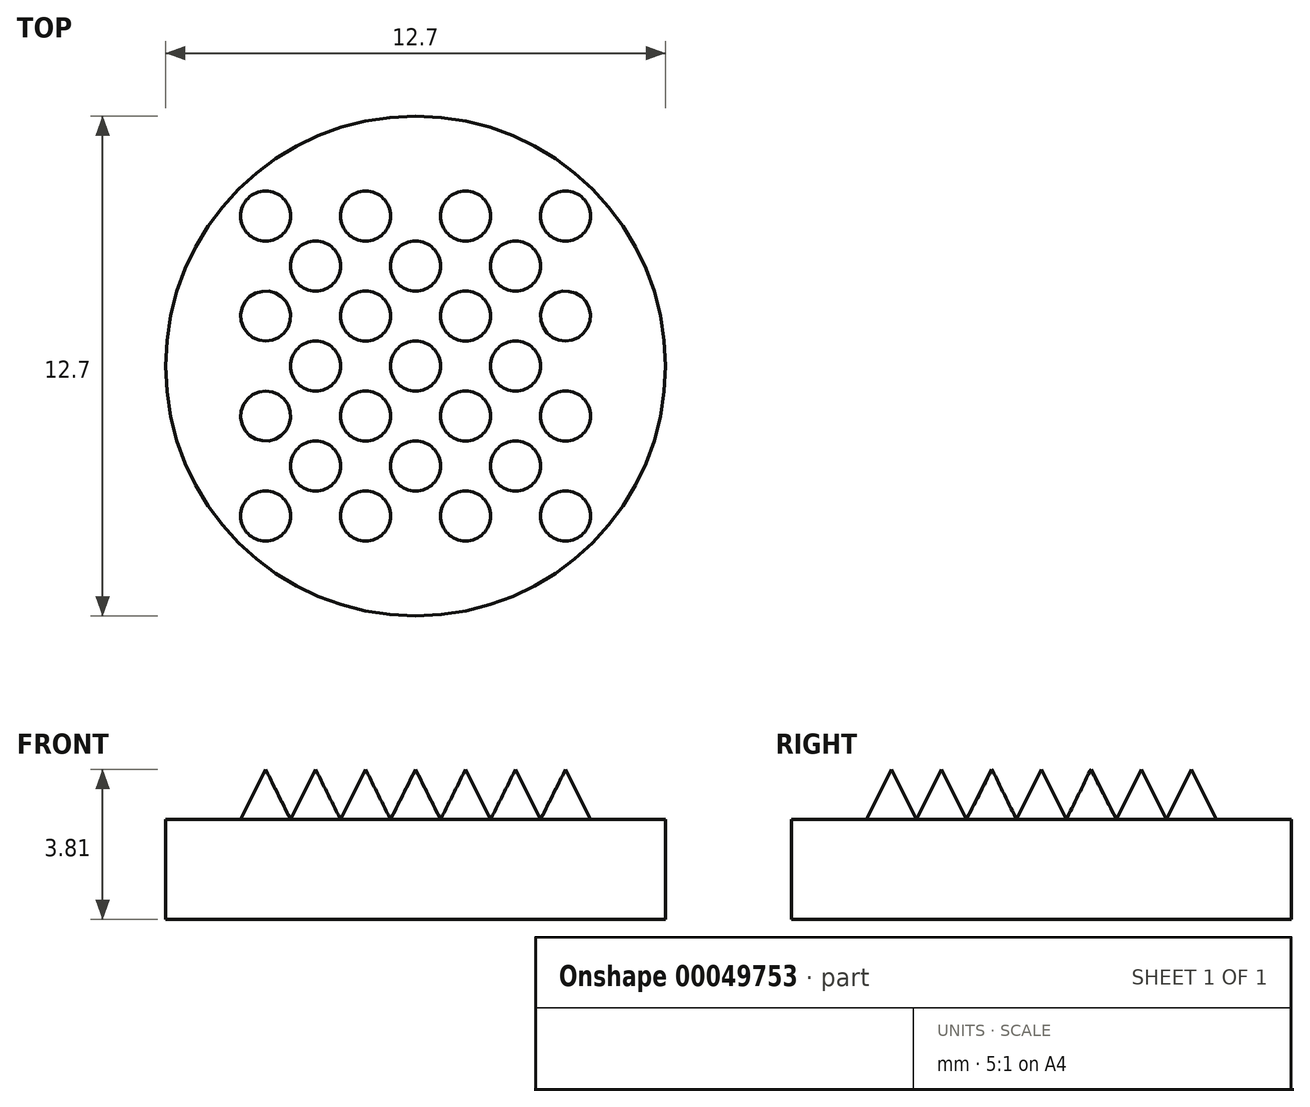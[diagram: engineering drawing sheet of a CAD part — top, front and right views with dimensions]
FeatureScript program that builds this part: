
annotation { "Feature Type Name" : "Feature", "Feature Type Description" : "" }
export const myFeature = defineFeature(function(context is Context, id is Id, definition is map)
    precondition{}
    {
        {
            var Q0;
            Q0=qCreatedBy(makeId("Top.planeOp"),FACE);
            var sketch = newSketch(context, id + "F0", { "sketchPlane" : qUnion([Q0])});
            skCircle(sketch, "E0", {"center": v(0, 0) * mm, "radius": 6.35 * mm});
            skSolve(sketch);
        }
        {
            var Q0;
            Q0=qCreatedBy(makeId("Top.planeOp"),FACE);
            var sketch = newSketch(context, id + "F1", { "sketchPlane" : qUnion([Q0])});
            skCircle(sketch, "E1", {"center": v(0, 0) * mm, "radius": 0.64 * mm});
            skCircle(sketch, "E2", {"center": v(1.27, 0) * mm, "radius": 0.64 * mm});
            skCircle(sketch, "E3", {"center": v(2.54, 0) * mm, "radius": 0.64 * mm});
            skCircle(sketch, "E4", {"center": v(1.27, -1.27) * mm, "radius": 0.64 * mm});
            skCircle(sketch, "E5", {"center": v(2.54, -1.27) * mm, "radius": 0.64 * mm});
            skCircle(sketch, "E6", {"center": v(1.27, -2.54) * mm, "radius": 0.64 * mm});
            skCircle(sketch, "E7", {"center": v(1.27, -3.81) * mm, "radius": 0.64 * mm});
            skCircle(sketch, "E8", {"center": v(2.54, -2.54) * mm, "radius": 0.64 * mm});
            skCircle(sketch, "E9", {"center": v(2.54, -3.81) * mm, "radius": 0.64 * mm});
            skCircle(sketch, "E10", {"center": v(0, -1.27) * mm, "radius": 0.64 * mm});
            skCircle(sketch, "E11", {"center": v(0, -2.54) * mm, "radius": 0.64 * mm});
            skCircle(sketch, "E12", {"center": v(0, -3.81) * mm, "radius": 0.64 * mm});
            skCircle(sketch, "E13", {"center": v(3.81, 0) * mm, "radius": 0.64 * mm});
            skCircle(sketch, "E14", {"center": v(3.81, -1.27) * mm, "radius": 0.64 * mm});
            skCircle(sketch, "E15", {"center": v(3.81, -2.54) * mm, "radius": 0.64 * mm});
            skCircle(sketch, "E16", {"center": v(3.81, -3.81) * mm, "radius": 0.64 * mm});
            skSolve(sketch);
        }
        {
            var Q0;
            Q0=makeQuery(id+"F1.imprint","IMPRINT",FACE,{"disambiguationData":[TD([[makeQuery(id+"F1.imprint","IMPRINT",EDGE,{"derivedFrom":sQuery(id+"F1.wireOp",EDGE,"E1")}),1.0]])]});
            cPlane(context, id + "F2", {"entities" : qUnion([Q0]), "cplaneType" : CPlaneType.OFFSET, "offset" : 1.27 * mm, "width" : 152.4 * mm, "height" : 152.4 * mm});
        }
        {
            var Q0;
            Q0=qCreatedBy(id+"F2.planeOp",FACE);
            var sketch = newSketch(context, id + "F3", { "sketchPlane" : qUnion([Q0])});
            skPoint(sketch, "E17", {"position": v(0, 0) * mm});
            skPoint(sketch, "E18", {"position": v(0, -1.27) * mm});
            skPoint(sketch, "E19", {"position": v(0, -2.54) * mm});
            skPoint(sketch, "E20", {"position": v(1.27, 0) * mm});
            skPoint(sketch, "E21", {"position": v(1.27, -1.27) * mm});
            skPoint(sketch, "E22", {"position": v(1.27, -2.54) * mm});
            skPoint(sketch, "E23", {"position": v(1.27, -3.81) * mm});
            skPoint(sketch, "E24", {"position": v(2.54, 0) * mm});
            skPoint(sketch, "E25", {"position": v(2.54, -1.27) * mm});
            skPoint(sketch, "E26", {"position": v(2.54, -2.54) * mm});
            skPoint(sketch, "E27", {"position": v(2.54, -3.81) * mm});
            skPoint(sketch, "E28", {"position": v(0, -3.81) * mm});
            skPoint(sketch, "E29", {"position": v(3.81, 0) * mm});
            skPoint(sketch, "E30", {"position": v(3.8, -1.25) * mm});
            skPoint(sketch, "E31", {"position": v(3.81, -2.51) * mm});
            skPoint(sketch, "E32", {"position": v(3.81, -3.81) * mm});
            skSolve(sketch);
        }
        {
            var Q0;
            {var subQ0=sQuery(id+"F1.wireOp",EDGE,"E1");var subQ1=makeQuery(id+"F1.imprint","INTERSECT",VERTEX,{"derivedFrom":[subQ0,sQuery(id+"F1.wireOp",EDGE,"E2")]});Q0=makeQuery(id+"F1.imprint","IMPRINT",FACE,{"disambiguationData":[TD([[makeQuery(id+"F1.imprint","IMPRINT",EDGE,{"disambiguationData":[TD([[subQ1,-1.0]])],"derivedFrom":subQ0}),1.0]])]});}
            var Q1;
            Q1=sQuery(id+"F3.wireOp",VERTEX,"E17");
            loft(context, id + "F4", {"sheetProfilesArray" : [{ "sheetProfileEntities" : qUnion([Q0]) }, { "sheetProfileEntities" : qUnion([Q1]) }]});
        }
        {
            var Q0;
            Q0=makeQuery(id+"F0.imprint","IMPRINT",FACE,{"disambiguationData":[TD([[makeQuery(id+"F0.imprint","IMPRINT",EDGE,{"derivedFrom":sQuery(id+"F0.wireOp",EDGE,"E0")}),1.0]])]});
            extrude(context, id + "F5", {"entities" : qUnion([Q0]), "oppositeDirection" : true, "depth" : 2.54 * mm});
        }
        {
            var Q1;
            {var subQ0=sQuery(id+"F1.wireOp",EDGE,"E11");var subQ1=makeQuery(id+"F1.imprint","INTERSECT",VERTEX,{"derivedFrom":[sQuery(id+"F1.wireOp",EDGE,"E10"),subQ0]});Q1=makeQuery(id+"F1.imprint","IMPRINT",FACE,{"disambiguationData":[TD([[makeQuery(id+"F1.imprint","IMPRINT",EDGE,{"disambiguationData":[TD([[subQ1,1.0]])],"derivedFrom":subQ0}),1.0]])]});}
            var Q2;
            Q2=sQuery(id+"F3.wireOp",VERTEX,"E19");
            loft(context, id + "F6", {"sheetProfilesArray" : [{ "sheetProfileEntities" : qUnion([Q1]) }, { "sheetProfileEntities" : qUnion([Q2]) }]});
        }
        {
            var Q1;
            {var subQ0=sQuery(id+"F1.wireOp",EDGE,"E4");var subQ1=makeQuery(id+"F1.imprint","INTERSECT",VERTEX,{"derivedFrom":[sQuery(id+"F1.wireOp",EDGE,"E2"),subQ0]});Q1=makeQuery(id+"F1.imprint","IMPRINT",FACE,{"disambiguationData":[TD([[makeQuery(id+"F1.imprint","IMPRINT",EDGE,{"disambiguationData":[TD([[subQ1,1.0]])],"derivedFrom":subQ0}),1.0]])]});}
            var Q2;
            Q2=sQuery(id+"F3.wireOp",VERTEX,"E21");
            loft(context, id + "F7", {"sheetProfilesArray" : [{ "sheetProfileEntities" : qUnion([Q1]) }, { "sheetProfileEntities" : qUnion([Q2]) }]});
        }
        {
            var Q1;
            {var subQ0=sQuery(id+"F1.wireOp",EDGE,"E7");var subQ1=makeQuery(id+"F1.imprint","INTERSECT",VERTEX,{"derivedFrom":[subQ0,sQuery(id+"F1.wireOp",EDGE,"E9")]});Q1=makeQuery(id+"F1.imprint","IMPRINT",FACE,{"disambiguationData":[TD([[makeQuery(id+"F1.imprint","IMPRINT",EDGE,{"disambiguationData":[TD([[subQ1,-1.0]])],"derivedFrom":subQ0}),1.0]])]});}
            var Q2;
            Q2=sQuery(id+"F3.wireOp",VERTEX,"E23");
            loft(context, id + "F8", {"sheetProfilesArray" : [{ "sheetProfileEntities" : qUnion([Q1]) }, { "sheetProfileEntities" : qUnion([Q2]) }]});
        }
        {
            var Q1;
            {var subQ0=sQuery(id+"F1.wireOp",EDGE,"E3");var subQ1=makeQuery(id+"F1.imprint","INTERSECT",VERTEX,{"derivedFrom":[sQuery(id+"F1.wireOp",EDGE,"E2"),subQ0]});Q1=makeQuery(id+"F1.imprint","IMPRINT",FACE,{"disambiguationData":[TD([[makeQuery(id+"F1.imprint","IMPRINT",EDGE,{"disambiguationData":[TD([[subQ1,-1.0]])],"derivedFrom":subQ0}),1.0]])]});}
            var Q2;
            Q2=sQuery(id+"F3.wireOp",VERTEX,"E24");
            loft(context, id + "F9", {"sheetProfilesArray" : [{ "sheetProfileEntities" : qUnion([Q1]) }, { "sheetProfileEntities" : qUnion([Q2]) }]});
        }
        {
            var Q1;
            {var subQ0=sQuery(id+"F1.wireOp",EDGE,"E8");var subQ1=makeQuery(id+"F1.imprint","INTERSECT",VERTEX,{"derivedFrom":[sQuery(id+"F1.wireOp",EDGE,"E5"),subQ0]});Q1=makeQuery(id+"F1.imprint","IMPRINT",FACE,{"disambiguationData":[TD([[makeQuery(id+"F1.imprint","IMPRINT",EDGE,{"disambiguationData":[TD([[subQ1,-1.0]])],"derivedFrom":subQ0}),1.0]])]});}
            var Q2;
            Q2=sQuery(id+"F3.wireOp",VERTEX,"E26");
            loft(context, id + "F10", {"sheetProfilesArray" : [{ "sheetProfileEntities" : qUnion([Q1]) }, { "sheetProfileEntities" : qUnion([Q2]) }]});
        }
        {
            var Q1;
            {var subQ0=sQuery(id+"F1.wireOp",EDGE,"E14");var subQ1=makeQuery(id+"F1.imprint","INTERSECT",VERTEX,{"derivedFrom":[sQuery(id+"F1.wireOp",EDGE,"E13"),subQ0]});Q1=makeQuery(id+"F1.imprint","IMPRINT",FACE,{"disambiguationData":[TD([[makeQuery(id+"F1.imprint","IMPRINT",EDGE,{"disambiguationData":[TD([[subQ1,-1.0]])],"derivedFrom":subQ0}),1.0]])]});}
            var Q2;
            Q2=sQuery(id+"F3.wireOp",VERTEX,"E30");
            loft(context, id + "F11", {"sheetProfilesArray" : [{ "sheetProfileEntities" : qUnion([Q1]) }, { "sheetProfileEntities" : qUnion([Q2]) }]});
        }
        {
            var Q1;
            {var subQ0=sQuery(id+"F1.wireOp",EDGE,"E16");var subQ1=makeQuery(id+"F1.imprint","INTERSECT",VERTEX,{"derivedFrom":[sQuery(id+"F1.wireOp",EDGE,"E9"),subQ0]});Q1=makeQuery(id+"F1.imprint","IMPRINT",FACE,{"disambiguationData":[TD([[makeQuery(id+"F1.imprint","IMPRINT",EDGE,{"disambiguationData":[TD([[subQ1,1.0]])],"derivedFrom":subQ0}),1.0]])]});}
            var Q2;
            Q2=sQuery(id+"F3.wireOp",VERTEX,"E32");
            loft(context, id + "F12", {"sheetProfilesArray" : [{ "sheetProfileEntities" : qUnion([Q1]) }, { "sheetProfileEntities" : qUnion([Q2]) }]});
        }
        {
            var Q0;
            {var subQ0=sQuery(id+"F1.wireOp",EDGE,"E1");var subQ1=makeQuery(id+"F1.imprint","INTERSECT",VERTEX,{"derivedFrom":[subQ0,sQuery(id+"F1.wireOp",EDGE,"E2")]});Q0=makeQuery(id+"F4.opLoft","SWEPT_BODY",BODY,{"disambiguationData":[OSD([makeQuery(id+"F1.imprint","IMPRINT",FACE,{"disambiguationData":[TD([[makeQuery(id+"F1.imprint","IMPRINT",EDGE,{"disambiguationData":[TD([[subQ1,-1.0]])],"derivedFrom":subQ0}),1.0]])]}),sQuery(id+"F3.wireOp",VERTEX,"E17")])]});}
            var Q1;
            {var subQ0=sQuery(id+"F1.wireOp",EDGE,"E10");var subQ1=makeQuery(id+"F1.imprint","INTERSECT",VERTEX,{"derivedFrom":[sQuery(id+"F1.wireOp",EDGE,"E1"),subQ0]});Q1=makeQuery(id+"F5vqhCHL6ANKIna_3.opLoft","SWEPT_BODY",BODY,{"disambiguationData":[OSD([makeQuery(id+"F1.imprint","IMPRINT",FACE,{"disambiguationData":[TD([[makeQuery(id+"F1.imprint","IMPRINT",EDGE,{"disambiguationData":[TD([[subQ1,1.0]])],"derivedFrom":subQ0}),1.0]])]}),sQuery(id+"F3.wireOp",VERTEX,"E18")])]});}
            var Q2;
            {var subQ0=sQuery(id+"F1.wireOp",EDGE,"E11");var subQ1=makeQuery(id+"F1.imprint","INTERSECT",VERTEX,{"derivedFrom":[sQuery(id+"F1.wireOp",EDGE,"E10"),subQ0]});Q2=makeQuery(id+"F6.opLoft","SWEPT_BODY",BODY,{"disambiguationData":[OSD([makeQuery(id+"F1.imprint","IMPRINT",FACE,{"disambiguationData":[TD([[makeQuery(id+"F1.imprint","IMPRINT",EDGE,{"disambiguationData":[TD([[subQ1,1.0]])],"derivedFrom":subQ0}),1.0]])]}),sQuery(id+"F3.wireOp",VERTEX,"E19")])]});}
            var Q3;
            {var subQ0=sQuery(id+"F1.wireOp",EDGE,"E12");var subQ1=makeQuery(id+"F1.imprint","INTERSECT",VERTEX,{"derivedFrom":[sQuery(id+"F1.wireOp",EDGE,"E7"),subQ0]});Q3=makeQuery(id+"FCgEybhU7v2E6e9_3.opLoft","SWEPT_BODY",BODY,{"disambiguationData":[OSD([makeQuery(id+"F1.imprint","IMPRINT",FACE,{"disambiguationData":[TD([[makeQuery(id+"F1.imprint","IMPRINT",EDGE,{"disambiguationData":[TD([[subQ1,-1.0]])],"derivedFrom":subQ0}),1.0]])]}),sQuery(id+"F3.wireOp",VERTEX,"E28")])]});}
            var Q4;
            {var subQ0=sQuery(id+"F1.wireOp",EDGE,"E7");var subQ1=makeQuery(id+"F1.imprint","INTERSECT",VERTEX,{"derivedFrom":[subQ0,sQuery(id+"F1.wireOp",EDGE,"E9")]});Q4=makeQuery(id+"F8.opLoft","SWEPT_BODY",BODY,{"disambiguationData":[OSD([makeQuery(id+"F1.imprint","IMPRINT",FACE,{"disambiguationData":[TD([[makeQuery(id+"F1.imprint","IMPRINT",EDGE,{"disambiguationData":[TD([[subQ1,-1.0]])],"derivedFrom":subQ0}),1.0]])]}),sQuery(id+"F3.wireOp",VERTEX,"E23")])]});}
            var Q5;
            {var subQ0=sQuery(id+"F1.wireOp",EDGE,"E6");var subQ1=makeQuery(id+"F1.imprint","INTERSECT",VERTEX,{"derivedFrom":[sQuery(id+"F1.wireOp",EDGE,"E4"),subQ0]});Q5=makeQuery(id+"FVhk51bG2k9nDs2_3.opLoft","SWEPT_BODY",BODY,{"disambiguationData":[OSD([makeQuery(id+"F1.imprint","IMPRINT",FACE,{"disambiguationData":[TD([[makeQuery(id+"F1.imprint","IMPRINT",EDGE,{"disambiguationData":[TD([[subQ1,1.0]])],"derivedFrom":subQ0}),1.0]])]}),sQuery(id+"F3.wireOp",VERTEX,"E22")])]});}
            var Q6;
            {var subQ0=sQuery(id+"F1.wireOp",EDGE,"E4");var subQ1=makeQuery(id+"F1.imprint","INTERSECT",VERTEX,{"derivedFrom":[sQuery(id+"F1.wireOp",EDGE,"E2"),subQ0]});Q6=makeQuery(id+"F7.opLoft","SWEPT_BODY",BODY,{"disambiguationData":[OSD([makeQuery(id+"F1.imprint","IMPRINT",FACE,{"disambiguationData":[TD([[makeQuery(id+"F1.imprint","IMPRINT",EDGE,{"disambiguationData":[TD([[subQ1,1.0]])],"derivedFrom":subQ0}),1.0]])]}),sQuery(id+"F3.wireOp",VERTEX,"E21")])]});}
            var Q7;
            {var subQ0=sQuery(id+"F1.wireOp",EDGE,"E2");var subQ1=makeQuery(id+"F1.imprint","INTERSECT",VERTEX,{"derivedFrom":[sQuery(id+"F1.wireOp",EDGE,"E1"),subQ0]});Q7=makeQuery(id+"F8jPV2Md5eXivMf_3.opLoft","SWEPT_BODY",BODY,{"disambiguationData":[OSD([makeQuery(id+"F1.imprint","IMPRINT",FACE,{"disambiguationData":[TD([[makeQuery(id+"F1.imprint","IMPRINT",EDGE,{"disambiguationData":[TD([[subQ1,1.0]])],"derivedFrom":subQ0}),1.0]])]}),sQuery(id+"F3.wireOp",VERTEX,"E20")])]});}
            var Q8;
            {var subQ0=sQuery(id+"F1.wireOp",EDGE,"E13");var subQ1=makeQuery(id+"F1.imprint","INTERSECT",VERTEX,{"derivedFrom":[sQuery(id+"F1.wireOp",EDGE,"E3"),subQ0]});Q8=makeQuery(id+"FrQLQlC9Cd4ulGg_3.opLoft","SWEPT_BODY",BODY,{"disambiguationData":[OSD([makeQuery(id+"F1.imprint","IMPRINT",FACE,{"disambiguationData":[TD([[makeQuery(id+"F1.imprint","IMPRINT",EDGE,{"disambiguationData":[TD([[subQ1,-1.0]])],"derivedFrom":subQ0}),1.0]])]}),sQuery(id+"F3.wireOp",VERTEX,"E29")])]});}
            var Q9;
            {var subQ0=sQuery(id+"F1.wireOp",EDGE,"E3");var subQ1=makeQuery(id+"F1.imprint","INTERSECT",VERTEX,{"derivedFrom":[sQuery(id+"F1.wireOp",EDGE,"E2"),subQ0]});Q9=makeQuery(id+"F9.opLoft","SWEPT_BODY",BODY,{"disambiguationData":[OSD([makeQuery(id+"F1.imprint","IMPRINT",FACE,{"disambiguationData":[TD([[makeQuery(id+"F1.imprint","IMPRINT",EDGE,{"disambiguationData":[TD([[subQ1,1.0]])],"derivedFrom":subQ0}),1.0]])]}),sQuery(id+"F3.wireOp",VERTEX,"E24")])]});}
            var Q10;
            {var subQ0=sQuery(id+"F1.wireOp",EDGE,"E5");var subQ1=makeQuery(id+"F1.imprint","INTERSECT",VERTEX,{"derivedFrom":[sQuery(id+"F1.wireOp",EDGE,"E3"),subQ0]});Q10=makeQuery(id+"FChkki0fDYVnrYv_3.opLoft","SWEPT_BODY",BODY,{"disambiguationData":[OSD([makeQuery(id+"F1.imprint","IMPRINT",FACE,{"disambiguationData":[TD([[makeQuery(id+"F1.imprint","IMPRINT",EDGE,{"disambiguationData":[TD([[subQ1,1.0]])],"derivedFrom":subQ0}),1.0]])]}),sQuery(id+"F3.wireOp",VERTEX,"E25")])]});}
            var Q11;
            {var subQ0=sQuery(id+"F1.wireOp",EDGE,"E14");var subQ1=makeQuery(id+"F1.imprint","INTERSECT",VERTEX,{"derivedFrom":[sQuery(id+"F1.wireOp",EDGE,"E13"),subQ0]});Q11=makeQuery(id+"F11.opLoft","SWEPT_BODY",BODY,{"disambiguationData":[OSD([makeQuery(id+"F1.imprint","IMPRINT",FACE,{"disambiguationData":[TD([[makeQuery(id+"F1.imprint","IMPRINT",EDGE,{"disambiguationData":[TD([[subQ1,-1.0]])],"derivedFrom":subQ0}),1.0]])]}),sQuery(id+"F3.wireOp",VERTEX,"E30")])]});}
            var Q12;
            {var subQ0=sQuery(id+"F1.wireOp",EDGE,"E15");var subQ1=makeQuery(id+"F1.imprint","INTERSECT",VERTEX,{"derivedFrom":[sQuery(id+"F1.wireOp",EDGE,"E14"),subQ0]});Q12=makeQuery(id+"Fu73TNwijkVTWP9_3.opLoft","SWEPT_BODY",BODY,{"disambiguationData":[OSD([makeQuery(id+"F1.imprint","IMPRINT",FACE,{"disambiguationData":[TD([[makeQuery(id+"F1.imprint","IMPRINT",EDGE,{"disambiguationData":[TD([[subQ1,-1.0]])],"derivedFrom":subQ0}),1.0]])]}),sQuery(id+"F3.wireOp",VERTEX,"E31")])]});}
            var Q13;
            {var subQ0=sQuery(id+"F1.wireOp",EDGE,"E8");var subQ1=makeQuery(id+"F1.imprint","INTERSECT",VERTEX,{"derivedFrom":[sQuery(id+"F1.wireOp",EDGE,"E5"),subQ0]});Q13=makeQuery(id+"F10.opLoft","SWEPT_BODY",BODY,{"disambiguationData":[OSD([makeQuery(id+"F1.imprint","IMPRINT",FACE,{"disambiguationData":[TD([[makeQuery(id+"F1.imprint","IMPRINT",EDGE,{"disambiguationData":[TD([[subQ1,1.0]])],"derivedFrom":subQ0}),1.0]])]}),sQuery(id+"F3.wireOp",VERTEX,"E26")])]});}
            var Q14;
            {var subQ0=sQuery(id+"F1.wireOp",EDGE,"E9");var subQ1=makeQuery(id+"F1.imprint","INTERSECT",VERTEX,{"derivedFrom":[subQ0,sQuery(id+"F1.wireOp",EDGE,"E16")]});Q14=makeQuery(id+"FI5Cp5ij7l5rHYo_3.opLoft","SWEPT_BODY",BODY,{"disambiguationData":[OSD([makeQuery(id+"F1.imprint","IMPRINT",FACE,{"disambiguationData":[TD([[makeQuery(id+"F1.imprint","IMPRINT",EDGE,{"disambiguationData":[TD([[subQ1,-1.0]])],"derivedFrom":subQ0}),1.0]])]}),sQuery(id+"F3.wireOp",VERTEX,"E27")])]});}
            var Q15;
            {var subQ0=sQuery(id+"F1.wireOp",EDGE,"E16");var subQ1=makeQuery(id+"F1.imprint","INTERSECT",VERTEX,{"derivedFrom":[sQuery(id+"F1.wireOp",EDGE,"E9"),subQ0]});Q15=makeQuery(id+"F12.opLoft","SWEPT_BODY",BODY,{"disambiguationData":[OSD([makeQuery(id+"F1.imprint","IMPRINT",FACE,{"disambiguationData":[TD([[makeQuery(id+"F1.imprint","IMPRINT",EDGE,{"disambiguationData":[TD([[subQ1,1.0]])],"derivedFrom":subQ0}),1.0]])]}),sQuery(id+"F3.wireOp",VERTEX,"E32")])]});}
            var Q16;
            Q16=qCreatedBy(makeId("Right.planeOp"),FACE);
            mirror(context, id + "F13", {"entities" : qUnion([Q0, Q1, Q2, Q3, Q4, Q5, Q6, Q7, Q8, Q9, Q10, Q11, Q12, Q13, Q14, Q15]), "mirrorPlane" : qUnion([Q16])});
        }
        {
            var Q0;
            {var subQ0=sQuery(id+"F1.wireOp",EDGE,"E13");var subQ1=makeQuery(id+"F1.imprint","INTERSECT",VERTEX,{"derivedFrom":[sQuery(id+"F1.wireOp",EDGE,"E3"),subQ0]});Q0=makeQuery(id+"F13.opPattern","COPY",BODY,{"derivedFrom":makeQuery(id+"FrQLQlC9Cd4ulGg_3.opLoft","SWEPT_BODY",BODY,{"disambiguationData":[OSD([makeQuery(id+"F1.imprint","IMPRINT",FACE,{"disambiguationData":[TD([[makeQuery(id+"F1.imprint","IMPRINT",EDGE,{"disambiguationData":[TD([[subQ1,-1.0]])],"derivedFrom":subQ0}),1.0]])]}),sQuery(id+"F3.wireOp",VERTEX,"E29")])]}),"instanceName":"1"});}
            var Q1;
            {var subQ0=sQuery(id+"F1.wireOp",EDGE,"E14");var subQ1=makeQuery(id+"F1.imprint","INTERSECT",VERTEX,{"derivedFrom":[sQuery(id+"F1.wireOp",EDGE,"E13"),subQ0]});Q1=makeQuery(id+"F13.opPattern","COPY",BODY,{"derivedFrom":makeQuery(id+"F11.opLoft","SWEPT_BODY",BODY,{"disambiguationData":[OSD([makeQuery(id+"F1.imprint","IMPRINT",FACE,{"disambiguationData":[TD([[makeQuery(id+"F1.imprint","IMPRINT",EDGE,{"disambiguationData":[TD([[subQ1,-1.0]])],"derivedFrom":subQ0}),1.0]])]}),sQuery(id+"F3.wireOp",VERTEX,"E30")])]}),"instanceName":"1"});}
            var Q2;
            {var subQ0=sQuery(id+"F1.wireOp",EDGE,"E15");var subQ1=makeQuery(id+"F1.imprint","INTERSECT",VERTEX,{"derivedFrom":[sQuery(id+"F1.wireOp",EDGE,"E14"),subQ0]});Q2=makeQuery(id+"F13.opPattern","COPY",BODY,{"derivedFrom":makeQuery(id+"Fu73TNwijkVTWP9_3.opLoft","SWEPT_BODY",BODY,{"disambiguationData":[OSD([makeQuery(id+"F1.imprint","IMPRINT",FACE,{"disambiguationData":[TD([[makeQuery(id+"F1.imprint","IMPRINT",EDGE,{"disambiguationData":[TD([[subQ1,-1.0]])],"derivedFrom":subQ0}),1.0]])]}),sQuery(id+"F3.wireOp",VERTEX,"E31")])]}),"instanceName":"1"});}
            var Q3;
            {var subQ0=sQuery(id+"F1.wireOp",EDGE,"E16");var subQ1=makeQuery(id+"F1.imprint","INTERSECT",VERTEX,{"derivedFrom":[sQuery(id+"F1.wireOp",EDGE,"E9"),subQ0]});Q3=makeQuery(id+"F13.opPattern","COPY",BODY,{"derivedFrom":makeQuery(id+"F12.opLoft","SWEPT_BODY",BODY,{"disambiguationData":[OSD([makeQuery(id+"F1.imprint","IMPRINT",FACE,{"disambiguationData":[TD([[makeQuery(id+"F1.imprint","IMPRINT",EDGE,{"disambiguationData":[TD([[subQ1,1.0]])],"derivedFrom":subQ0}),1.0]])]}),sQuery(id+"F3.wireOp",VERTEX,"E32")])]}),"instanceName":"1"});}
            var Q4;
            {var subQ0=sQuery(id+"F1.wireOp",EDGE,"E9");var subQ1=makeQuery(id+"F1.imprint","INTERSECT",VERTEX,{"derivedFrom":[subQ0,sQuery(id+"F1.wireOp",EDGE,"E16")]});Q4=makeQuery(id+"F13.opPattern","COPY",BODY,{"derivedFrom":makeQuery(id+"FI5Cp5ij7l5rHYo_3.opLoft","SWEPT_BODY",BODY,{"disambiguationData":[OSD([makeQuery(id+"F1.imprint","IMPRINT",FACE,{"disambiguationData":[TD([[makeQuery(id+"F1.imprint","IMPRINT",EDGE,{"disambiguationData":[TD([[subQ1,-1.0]])],"derivedFrom":subQ0}),1.0]])]}),sQuery(id+"F3.wireOp",VERTEX,"E27")])]}),"instanceName":"1"});}
            var Q5;
            {var subQ0=sQuery(id+"F1.wireOp",EDGE,"E8");var subQ1=makeQuery(id+"F1.imprint","INTERSECT",VERTEX,{"derivedFrom":[sQuery(id+"F1.wireOp",EDGE,"E5"),subQ0]});Q5=makeQuery(id+"F13.opPattern","COPY",BODY,{"derivedFrom":makeQuery(id+"F10.opLoft","SWEPT_BODY",BODY,{"disambiguationData":[OSD([makeQuery(id+"F1.imprint","IMPRINT",FACE,{"disambiguationData":[TD([[makeQuery(id+"F1.imprint","IMPRINT",EDGE,{"disambiguationData":[TD([[subQ1,1.0]])],"derivedFrom":subQ0}),1.0]])]}),sQuery(id+"F3.wireOp",VERTEX,"E26")])]}),"instanceName":"1"});}
            var Q6;
            {var subQ0=sQuery(id+"F1.wireOp",EDGE,"E5");var subQ1=makeQuery(id+"F1.imprint","INTERSECT",VERTEX,{"derivedFrom":[sQuery(id+"F1.wireOp",EDGE,"E3"),subQ0]});Q6=makeQuery(id+"F13.opPattern","COPY",BODY,{"derivedFrom":makeQuery(id+"FChkki0fDYVnrYv_3.opLoft","SWEPT_BODY",BODY,{"disambiguationData":[OSD([makeQuery(id+"F1.imprint","IMPRINT",FACE,{"disambiguationData":[TD([[makeQuery(id+"F1.imprint","IMPRINT",EDGE,{"disambiguationData":[TD([[subQ1,1.0]])],"derivedFrom":subQ0}),1.0]])]}),sQuery(id+"F3.wireOp",VERTEX,"E25")])]}),"instanceName":"1"});}
            var Q7;
            {var subQ0=sQuery(id+"F1.wireOp",EDGE,"E3");var subQ1=makeQuery(id+"F1.imprint","INTERSECT",VERTEX,{"derivedFrom":[sQuery(id+"F1.wireOp",EDGE,"E2"),subQ0]});Q7=makeQuery(id+"F13.opPattern","COPY",BODY,{"derivedFrom":makeQuery(id+"F9.opLoft","SWEPT_BODY",BODY,{"disambiguationData":[OSD([makeQuery(id+"F1.imprint","IMPRINT",FACE,{"disambiguationData":[TD([[makeQuery(id+"F1.imprint","IMPRINT",EDGE,{"disambiguationData":[TD([[subQ1,1.0]])],"derivedFrom":subQ0}),1.0]])]}),sQuery(id+"F3.wireOp",VERTEX,"E24")])]}),"instanceName":"1"});}
            var Q8;
            {var subQ0=sQuery(id+"F1.wireOp",EDGE,"E2");var subQ1=makeQuery(id+"F1.imprint","INTERSECT",VERTEX,{"derivedFrom":[sQuery(id+"F1.wireOp",EDGE,"E1"),subQ0]});Q8=makeQuery(id+"F13.opPattern","COPY",BODY,{"derivedFrom":makeQuery(id+"F8jPV2Md5eXivMf_3.opLoft","SWEPT_BODY",BODY,{"disambiguationData":[OSD([makeQuery(id+"F1.imprint","IMPRINT",FACE,{"disambiguationData":[TD([[makeQuery(id+"F1.imprint","IMPRINT",EDGE,{"disambiguationData":[TD([[subQ1,1.0]])],"derivedFrom":subQ0}),1.0]])]}),sQuery(id+"F3.wireOp",VERTEX,"E20")])]}),"instanceName":"1"});}
            var Q9;
            {var subQ0=sQuery(id+"F1.wireOp",EDGE,"E4");var subQ1=makeQuery(id+"F1.imprint","INTERSECT",VERTEX,{"derivedFrom":[sQuery(id+"F1.wireOp",EDGE,"E2"),subQ0]});Q9=makeQuery(id+"F13.opPattern","COPY",BODY,{"derivedFrom":makeQuery(id+"F7.opLoft","SWEPT_BODY",BODY,{"disambiguationData":[OSD([makeQuery(id+"F1.imprint","IMPRINT",FACE,{"disambiguationData":[TD([[makeQuery(id+"F1.imprint","IMPRINT",EDGE,{"disambiguationData":[TD([[subQ1,1.0]])],"derivedFrom":subQ0}),1.0]])]}),sQuery(id+"F3.wireOp",VERTEX,"E21")])]}),"instanceName":"1"});}
            var Q10;
            {var subQ0=sQuery(id+"F1.wireOp",EDGE,"E6");var subQ1=makeQuery(id+"F1.imprint","INTERSECT",VERTEX,{"derivedFrom":[sQuery(id+"F1.wireOp",EDGE,"E4"),subQ0]});Q10=makeQuery(id+"F13.opPattern","COPY",BODY,{"derivedFrom":makeQuery(id+"FVhk51bG2k9nDs2_3.opLoft","SWEPT_BODY",BODY,{"disambiguationData":[OSD([makeQuery(id+"F1.imprint","IMPRINT",FACE,{"disambiguationData":[TD([[makeQuery(id+"F1.imprint","IMPRINT",EDGE,{"disambiguationData":[TD([[subQ1,1.0]])],"derivedFrom":subQ0}),1.0]])]}),sQuery(id+"F3.wireOp",VERTEX,"E22")])]}),"instanceName":"1"});}
            var Q11;
            {var subQ0=sQuery(id+"F1.wireOp",EDGE,"E7");var subQ1=makeQuery(id+"F1.imprint","INTERSECT",VERTEX,{"derivedFrom":[subQ0,sQuery(id+"F1.wireOp",EDGE,"E9")]});Q11=makeQuery(id+"F13.opPattern","COPY",BODY,{"derivedFrom":makeQuery(id+"F8.opLoft","SWEPT_BODY",BODY,{"disambiguationData":[OSD([makeQuery(id+"F1.imprint","IMPRINT",FACE,{"disambiguationData":[TD([[makeQuery(id+"F1.imprint","IMPRINT",EDGE,{"disambiguationData":[TD([[subQ1,-1.0]])],"derivedFrom":subQ0}),1.0]])]}),sQuery(id+"F3.wireOp",VERTEX,"E23")])]}),"instanceName":"1"});}
            var Q12;
            {var subQ0=sQuery(id+"F1.wireOp",EDGE,"E12");var subQ1=makeQuery(id+"F1.imprint","INTERSECT",VERTEX,{"derivedFrom":[sQuery(id+"F1.wireOp",EDGE,"E7"),subQ0]});Q12=makeQuery(id+"FCgEybhU7v2E6e9_3.opLoft","SWEPT_BODY",BODY,{"disambiguationData":[OSD([makeQuery(id+"F1.imprint","IMPRINT",FACE,{"disambiguationData":[TD([[makeQuery(id+"F1.imprint","IMPRINT",EDGE,{"disambiguationData":[TD([[subQ1,-1.0]])],"derivedFrom":subQ0}),1.0]])]}),sQuery(id+"F3.wireOp",VERTEX,"E28")])]});}
            var Q13;
            {var subQ0=sQuery(id+"F1.wireOp",EDGE,"E11");var subQ1=makeQuery(id+"F1.imprint","INTERSECT",VERTEX,{"derivedFrom":[sQuery(id+"F1.wireOp",EDGE,"E10"),subQ0]});Q13=makeQuery(id+"F6.opLoft","SWEPT_BODY",BODY,{"disambiguationData":[OSD([makeQuery(id+"F1.imprint","IMPRINT",FACE,{"disambiguationData":[TD([[makeQuery(id+"F1.imprint","IMPRINT",EDGE,{"disambiguationData":[TD([[subQ1,1.0]])],"derivedFrom":subQ0}),1.0]])]}),sQuery(id+"F3.wireOp",VERTEX,"E19")])]});}
            var Q14;
            {var subQ0=sQuery(id+"F1.wireOp",EDGE,"E10");var subQ1=makeQuery(id+"F1.imprint","INTERSECT",VERTEX,{"derivedFrom":[sQuery(id+"F1.wireOp",EDGE,"E1"),subQ0]});Q14=makeQuery(id+"F5vqhCHL6ANKIna_3.opLoft","SWEPT_BODY",BODY,{"disambiguationData":[OSD([makeQuery(id+"F1.imprint","IMPRINT",FACE,{"disambiguationData":[TD([[makeQuery(id+"F1.imprint","IMPRINT",EDGE,{"disambiguationData":[TD([[subQ1,1.0]])],"derivedFrom":subQ0}),1.0]])]}),sQuery(id+"F3.wireOp",VERTEX,"E18")])]});}
            var Q15;
            {var subQ0=sQuery(id+"F1.wireOp",EDGE,"E1");var subQ1=makeQuery(id+"F1.imprint","INTERSECT",VERTEX,{"derivedFrom":[subQ0,sQuery(id+"F1.wireOp",EDGE,"E2")]});Q15=makeQuery(id+"F4.opLoft","SWEPT_BODY",BODY,{"disambiguationData":[OSD([makeQuery(id+"F1.imprint","IMPRINT",FACE,{"disambiguationData":[TD([[makeQuery(id+"F1.imprint","IMPRINT",EDGE,{"disambiguationData":[TD([[subQ1,-1.0]])],"derivedFrom":subQ0}),1.0]])]}),sQuery(id+"F3.wireOp",VERTEX,"E17")])]});}
            var Q16;
            {var subQ0=sQuery(id+"F1.wireOp",EDGE,"E2");var subQ1=makeQuery(id+"F1.imprint","INTERSECT",VERTEX,{"derivedFrom":[sQuery(id+"F1.wireOp",EDGE,"E1"),subQ0]});Q16=makeQuery(id+"F8jPV2Md5eXivMf_3.opLoft","SWEPT_BODY",BODY,{"disambiguationData":[OSD([makeQuery(id+"F1.imprint","IMPRINT",FACE,{"disambiguationData":[TD([[makeQuery(id+"F1.imprint","IMPRINT",EDGE,{"disambiguationData":[TD([[subQ1,1.0]])],"derivedFrom":subQ0}),1.0]])]}),sQuery(id+"F3.wireOp",VERTEX,"E20")])]});}
            var Q17;
            {var subQ0=sQuery(id+"F1.wireOp",EDGE,"E3");var subQ1=makeQuery(id+"F1.imprint","INTERSECT",VERTEX,{"derivedFrom":[sQuery(id+"F1.wireOp",EDGE,"E2"),subQ0]});Q17=makeQuery(id+"F9.opLoft","SWEPT_BODY",BODY,{"disambiguationData":[OSD([makeQuery(id+"F1.imprint","IMPRINT",FACE,{"disambiguationData":[TD([[makeQuery(id+"F1.imprint","IMPRINT",EDGE,{"disambiguationData":[TD([[subQ1,1.0]])],"derivedFrom":subQ0}),1.0]])]}),sQuery(id+"F3.wireOp",VERTEX,"E24")])]});}
            var Q18;
            {var subQ0=sQuery(id+"F1.wireOp",EDGE,"E13");var subQ1=makeQuery(id+"F1.imprint","INTERSECT",VERTEX,{"derivedFrom":[sQuery(id+"F1.wireOp",EDGE,"E3"),subQ0]});Q18=makeQuery(id+"FrQLQlC9Cd4ulGg_3.opLoft","SWEPT_BODY",BODY,{"disambiguationData":[OSD([makeQuery(id+"F1.imprint","IMPRINT",FACE,{"disambiguationData":[TD([[makeQuery(id+"F1.imprint","IMPRINT",EDGE,{"disambiguationData":[TD([[subQ1,-1.0]])],"derivedFrom":subQ0}),1.0]])]}),sQuery(id+"F3.wireOp",VERTEX,"E29")])]});}
            var Q19;
            {var subQ0=sQuery(id+"F1.wireOp",EDGE,"E14");var subQ1=makeQuery(id+"F1.imprint","INTERSECT",VERTEX,{"derivedFrom":[sQuery(id+"F1.wireOp",EDGE,"E13"),subQ0]});Q19=makeQuery(id+"F11.opLoft","SWEPT_BODY",BODY,{"disambiguationData":[OSD([makeQuery(id+"F1.imprint","IMPRINT",FACE,{"disambiguationData":[TD([[makeQuery(id+"F1.imprint","IMPRINT",EDGE,{"disambiguationData":[TD([[subQ1,-1.0]])],"derivedFrom":subQ0}),1.0]])]}),sQuery(id+"F3.wireOp",VERTEX,"E30")])]});}
            var Q20;
            {var subQ0=sQuery(id+"F1.wireOp",EDGE,"E5");var subQ1=makeQuery(id+"F1.imprint","INTERSECT",VERTEX,{"derivedFrom":[sQuery(id+"F1.wireOp",EDGE,"E3"),subQ0]});Q20=makeQuery(id+"FChkki0fDYVnrYv_3.opLoft","SWEPT_BODY",BODY,{"disambiguationData":[OSD([makeQuery(id+"F1.imprint","IMPRINT",FACE,{"disambiguationData":[TD([[makeQuery(id+"F1.imprint","IMPRINT",EDGE,{"disambiguationData":[TD([[subQ1,1.0]])],"derivedFrom":subQ0}),1.0]])]}),sQuery(id+"F3.wireOp",VERTEX,"E25")])]});}
            var Q21;
            {var subQ0=sQuery(id+"F1.wireOp",EDGE,"E4");var subQ1=makeQuery(id+"F1.imprint","INTERSECT",VERTEX,{"derivedFrom":[sQuery(id+"F1.wireOp",EDGE,"E2"),subQ0]});Q21=makeQuery(id+"F7.opLoft","SWEPT_BODY",BODY,{"disambiguationData":[OSD([makeQuery(id+"F1.imprint","IMPRINT",FACE,{"disambiguationData":[TD([[makeQuery(id+"F1.imprint","IMPRINT",EDGE,{"disambiguationData":[TD([[subQ1,1.0]])],"derivedFrom":subQ0}),1.0]])]}),sQuery(id+"F3.wireOp",VERTEX,"E21")])]});}
            var Q22;
            {var subQ0=sQuery(id+"F1.wireOp",EDGE,"E6");var subQ1=makeQuery(id+"F1.imprint","INTERSECT",VERTEX,{"derivedFrom":[sQuery(id+"F1.wireOp",EDGE,"E4"),subQ0]});Q22=makeQuery(id+"FVhk51bG2k9nDs2_3.opLoft","SWEPT_BODY",BODY,{"disambiguationData":[OSD([makeQuery(id+"F1.imprint","IMPRINT",FACE,{"disambiguationData":[TD([[makeQuery(id+"F1.imprint","IMPRINT",EDGE,{"disambiguationData":[TD([[subQ1,1.0]])],"derivedFrom":subQ0}),1.0]])]}),sQuery(id+"F3.wireOp",VERTEX,"E22")])]});}
            var Q23;
            {var subQ0=sQuery(id+"F1.wireOp",EDGE,"E8");var subQ1=makeQuery(id+"F1.imprint","INTERSECT",VERTEX,{"derivedFrom":[sQuery(id+"F1.wireOp",EDGE,"E5"),subQ0]});Q23=makeQuery(id+"F10.opLoft","SWEPT_BODY",BODY,{"disambiguationData":[OSD([makeQuery(id+"F1.imprint","IMPRINT",FACE,{"disambiguationData":[TD([[makeQuery(id+"F1.imprint","IMPRINT",EDGE,{"disambiguationData":[TD([[subQ1,1.0]])],"derivedFrom":subQ0}),1.0]])]}),sQuery(id+"F3.wireOp",VERTEX,"E26")])]});}
            var Q24;
            {var subQ0=sQuery(id+"F1.wireOp",EDGE,"E15");var subQ1=makeQuery(id+"F1.imprint","INTERSECT",VERTEX,{"derivedFrom":[sQuery(id+"F1.wireOp",EDGE,"E14"),subQ0]});Q24=makeQuery(id+"Fu73TNwijkVTWP9_3.opLoft","SWEPT_BODY",BODY,{"disambiguationData":[OSD([makeQuery(id+"F1.imprint","IMPRINT",FACE,{"disambiguationData":[TD([[makeQuery(id+"F1.imprint","IMPRINT",EDGE,{"disambiguationData":[TD([[subQ1,-1.0]])],"derivedFrom":subQ0}),1.0]])]}),sQuery(id+"F3.wireOp",VERTEX,"E31")])]});}
            var Q25;
            {var subQ0=sQuery(id+"F1.wireOp",EDGE,"E16");var subQ1=makeQuery(id+"F1.imprint","INTERSECT",VERTEX,{"derivedFrom":[sQuery(id+"F1.wireOp",EDGE,"E9"),subQ0]});Q25=makeQuery(id+"F12.opLoft","SWEPT_BODY",BODY,{"disambiguationData":[OSD([makeQuery(id+"F1.imprint","IMPRINT",FACE,{"disambiguationData":[TD([[makeQuery(id+"F1.imprint","IMPRINT",EDGE,{"disambiguationData":[TD([[subQ1,1.0]])],"derivedFrom":subQ0}),1.0]])]}),sQuery(id+"F3.wireOp",VERTEX,"E32")])]});}
            var Q26;
            {var subQ0=sQuery(id+"F1.wireOp",EDGE,"E9");var subQ1=makeQuery(id+"F1.imprint","INTERSECT",VERTEX,{"derivedFrom":[subQ0,sQuery(id+"F1.wireOp",EDGE,"E16")]});Q26=makeQuery(id+"FI5Cp5ij7l5rHYo_3.opLoft","SWEPT_BODY",BODY,{"disambiguationData":[OSD([makeQuery(id+"F1.imprint","IMPRINT",FACE,{"disambiguationData":[TD([[makeQuery(id+"F1.imprint","IMPRINT",EDGE,{"disambiguationData":[TD([[subQ1,-1.0]])],"derivedFrom":subQ0}),1.0]])]}),sQuery(id+"F3.wireOp",VERTEX,"E27")])]});}
            var Q27;
            {var subQ0=sQuery(id+"F1.wireOp",EDGE,"E7");var subQ1=makeQuery(id+"F1.imprint","INTERSECT",VERTEX,{"derivedFrom":[subQ0,sQuery(id+"F1.wireOp",EDGE,"E9")]});Q27=makeQuery(id+"F8.opLoft","SWEPT_BODY",BODY,{"disambiguationData":[OSD([makeQuery(id+"F1.imprint","IMPRINT",FACE,{"disambiguationData":[TD([[makeQuery(id+"F1.imprint","IMPRINT",EDGE,{"disambiguationData":[TD([[subQ1,-1.0]])],"derivedFrom":subQ0}),1.0]])]}),sQuery(id+"F3.wireOp",VERTEX,"E23")])]});}
            var Q28;
            Q28=qCreatedBy(makeId("Front.planeOp"),FACE);
            mirror(context, id + "F14", {"entities" : qUnion([Q0, Q1, Q2, Q3, Q4, Q5, Q6, Q7, Q8, Q9, Q10, Q11, Q12, Q13, Q14, Q15, Q16, Q17, Q18, Q19, Q20, Q21, Q22, Q23, Q24, Q25, Q26, Q27]), "mirrorPlane" : qUnion([Q28])});
        }
    });
